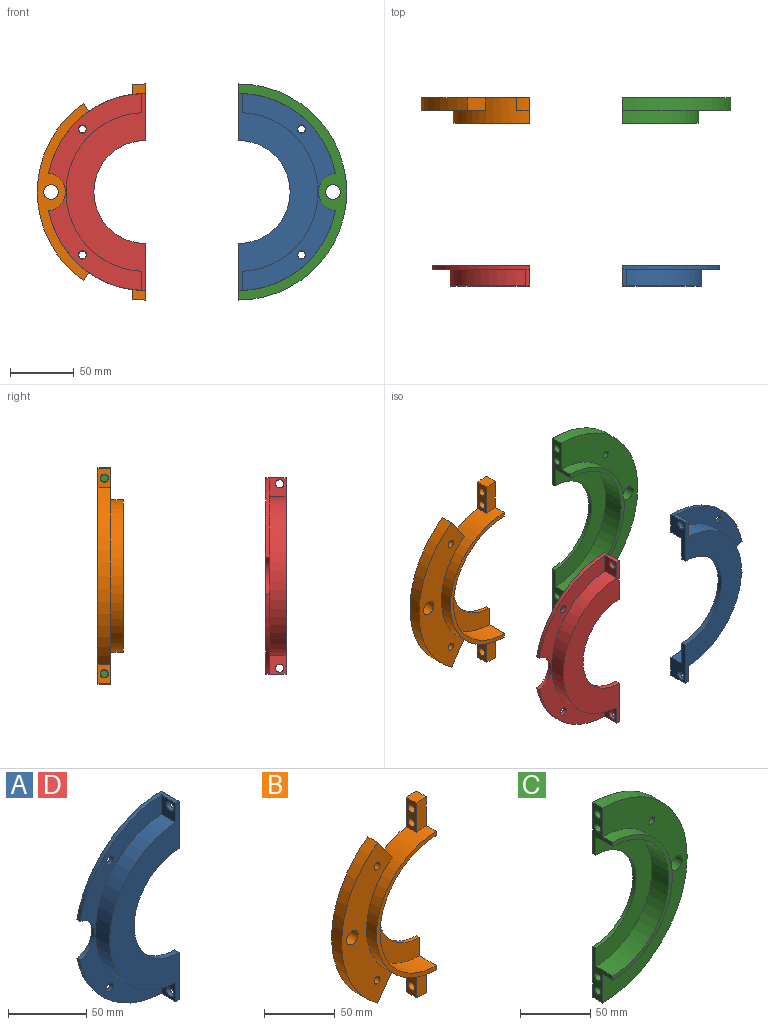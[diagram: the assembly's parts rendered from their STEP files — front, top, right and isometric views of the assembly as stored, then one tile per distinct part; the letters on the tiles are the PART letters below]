
ASSEMBLY  parts=4 mates=7
PART A: 22 faces, bbox 76.1x16x155 mm
  f0: plane 3x0.06mm, normal (0,-1,0), area 0mm2, adj f5,f19
  f1: plane 154.88x73.06mm, normal (0,-1,0), area 2813.3mm2, adj f3,f4,f5,f13,f14,f15,f16,f18
  f2: plane 3x0.06mm, normal (0,-1,0), area 0mm2, adj f4,f17
  f3: cylinder r=62.5mm len=124.86mm, axis (0,-1,0), area 2474.5mm2, adj f1,f6,f16,f18
  f4: cylinder r=77.5mm len=76.06mm, axis (0,1,0), area 320.2mm2, adj f1,f2,f8,f11,f13
  f5: cylinder r=77.5mm len=76.06mm, axis (0,1,0), area 320.2mm2, adj f0,f1,f8,f12,f13
  f6: plane 155x62.5mm, normal (0,-1,0), area 3649.4mm2, adj f3,f7,f11,f12,f16,f17,f18,f19
  f7: cylinder r=40.5mm len=81mm, axis (0,1,0), area 508.9mm2, adj f6,f10,f11,f12
  f8: plane 155x76.06mm, normal (0,1,0), area 3337.2mm2, adj f4,f5,f9,f11,f12,f13,f14,f15
  f9: cylinder r=60.25mm len=120.5mm, axis (0,1,0), area 2271.4mm2, adj f8,f10,f11,f12
  f10: plane 120.5x60.25mm, normal (0,1,0), area 3125.6mm2, adj f7,f9,f11,f12
  f11: plane 37x16mm, normal (1,0,0), area 321.8mm2, adj f4,f6,f7,f8,f9,f10,f17,f21
  f12: plane 37x16mm, normal (1,0,0), area 321.8mm2, adj f5,f6,f7,f8,f9,f10,f19,f20
  f13: cylinder r=15mm len=29.79mm, axis (0,-1,0), area 130.7mm2, adj f1,f4,f5,f8
  f14: cylinder r=3.25mm len=6.5mm, axis (0,-1,0), area 61.3mm2, adj f1,f8
  f15: cylinder r=3.25mm len=6.5mm, axis (0,-1,0), area 61.3mm2, adj f1,f8
  f16: plane 15.01x13mm, normal (-1,0,0), area 162mm2, adj f1,f3,f6,f17,f21
  f17: plane 13x3mm, normal (-0.02,0,1), area 39mm2, adj f2,f6,f11,f16
  f18: plane 15.01x13mm, normal (-1,0,0), area 162mm2, adj f1,f3,f6,f19,f20
  f19: plane 13x3mm, normal (-0.02,0,-1), area 39mm2, adj f0,f6,f12,f18
  f20: cylinder r=3.25mm len=6.5mm, axis (1,0,0), area 61.3mm2, adj f12,f18
  f21: cylinder r=3.25mm len=6.5mm, axis (1,0,0), area 61.3mm2, adj f11,f16
PART B: 25 faces, bbox 85x20x170 mm
  f0: cylinder r=85mm len=139.26mm, axis (0,1,0), area 1631.9mm2, adj f2,f4,f18,f19
  f1: cylinder r=85mm len=10mm, axis (0,1,0), area 100.2mm2, adj f3,f4,f6,f17
  f2: plane 139.26x50.59mm, normal (0,-1,0), area 3319.3mm2, adj f0,f9,f10,f11,f13,f18,f19
  f3: plane 25.84x10mm, normal (0,-1,0), area 250.8mm2, adj f1,f6,f13,f17
  f4: plane 170x85mm, normal (0,1,0), area 6899.3mm2, adj f0,f1,f5,f6,f7,f8,f9,f10
  f5: plane 44.5x20mm, normal (1,0,0), area 301.6mm2, adj f4,f7,f8,f12,f13,f14,f15,f16
  f6: plane 44.5x20mm, normal (1,0,0), area 301.6mm2, adj f1,f3,f4,f7,f13,f14,f15,f16
  f7: cylinder r=40.5mm len=81mm, axis (0,1,0), area 381.7mm2, adj f4,f5,f6,f16
  f8: cylinder r=85mm len=10mm, axis (0,1,0), area 100.2mm2, adj f4,f5,f12,f20
  f9: cylinder r=3mm len=10mm, axis (0,1,0), area 188.5mm2, adj f2,f4
  f10: cylinder r=5.75mm len=11.5mm, axis (0,1,0), area 361.3mm2, adj f2,f4
  f11: cylinder r=3mm len=10mm, axis (0,1,0), area 188.5mm2, adj f2,f4
  f12: plane 25.84x10mm, normal (0,-1,0), area 250.8mm2, adj f5,f8,f13,f20
  f13: cylinder r=60mm len=120mm, axis (0,1,0), area 2417.1mm2, adj f2,f3,f4,f5,f6,f12,f14,f17
  f14: plane 120x60mm, normal (0,-1,0), area 640.5mm2, adj f5,f6,f13,f15
  f15: cylinder r=56.5mm len=113mm, axis (0,-1,0), area 3017.5mm2, adj f5,f6,f14,f16
  f16: plane 113x56.5mm, normal (0,-1,0), area 2437.9mm2, adj f5,f6,f7,f15
  f17: plane 25.25x10mm, normal (-1,0,0), area 186.1mm2, adj f1,f3,f4,f13,f23,f24
  f18: plane 20.48x14.34mm, normal (0.82,0,-0.57), area 250mm2, adj f0,f2,f4,f13
  f19: plane 20.48x14.34mm, normal (0.82,0,0.57), area 250mm2, adj f0,f2,f4,f13
  f20: plane 25.25x10mm, normal (-1,0,0), area 186.1mm2, adj f4,f8,f12,f13,f21,f22
  f21: cylinder r=3.25mm len=10mm, axis (1,0,0), area 204.2mm2, adj f5,f20
  f22: cylinder r=3.25mm len=10mm, axis (1,0,0), area 204.2mm2, adj f5,f20
  f23: cylinder r=3.25mm len=10mm, axis (1,0,0), area 204.2mm2, adj f6,f17
  f24: cylinder r=3.25mm len=10mm, axis (1,0,0), area 204.2mm2, adj f6,f17
PART C: 21 faces, bbox 85x20x170 mm
  f0: plane 44.5x20mm, normal (-1,0,0), area 311.5mm2, adj f1,f2,f7,f8,f9,f10,f11,f12
  f1: cylinder r=40.5mm len=81mm, axis (0,1,0), area 381.7mm2, adj f0,f3,f8,f12
  f2: cylinder r=85mm len=170mm, axis (0,1,0), area 2670.4mm2, adj f0,f3,f7,f8
  f3: plane 44.5x20mm, normal (-1,0,0), area 311.5mm2, adj f1,f2,f7,f8,f9,f10,f11,f12
  f4: cylinder r=5.75mm len=11.5mm, axis (0,1,0), area 361.3mm2, adj f7,f8
  f5: cylinder r=3mm len=10mm, axis (0,1,0), area 188.5mm2, adj f7,f8
  f6: cylinder r=3mm len=10mm, axis (0,1,0), area 188.5mm2, adj f7,f8
  f7: plane 170x85mm, normal (0,-1,0), area 5533.7mm2, adj f0,f2,f3,f4,f5,f6,f9
  f8: plane 170x85mm, normal (0,1,0), area 8612.1mm2, adj f0,f1,f2,f3,f4,f5,f6
  f9: cylinder r=60mm len=120mm, axis (0,1,0), area 1885mm2, adj f0,f3,f7,f10
  f10: plane 120x60mm, normal (0,-1,0), area 640.5mm2, adj f0,f3,f9,f11
  f11: cylinder r=56.5mm len=113mm, axis (0,-1,0), area 3017.5mm2, adj f0,f3,f10,f12
  f12: plane 113x56.5mm, normal (0,-1,0), area 2437.9mm2, adj f0,f1,f3,f11
  f13: cylinder r=3mm len=20mm, axis (-1,0,0), area 377mm2, adj f3,f14
  f14: plane 6x6mm, normal (-1,0,0), area 28.3mm2, adj f13
  f15: cylinder r=3mm len=20mm, axis (-1,0,0), area 377mm2, adj f3,f16
  f16: plane 6x6mm, normal (-1,0,0), area 28.3mm2, adj f15
  f17: cylinder r=3mm len=20mm, axis (-1,0,0), area 377mm2, adj f0,f18
  f18: plane 6x6mm, normal (-1,0,0), area 28.3mm2, adj f17
  f19: cylinder r=3mm len=20mm, axis (-1,0,0), area 377mm2, adj f0,f20
  f20: plane 6x6mm, normal (-1,0,0), area 28.3mm2, adj f19
PART D: same geometry as A
PLACE A rot(axis=(0,1,0),180deg) t=(165.07,-127.15,37.54)mm
PLACE B t=(91.67,4.83,37.54)mm fixed
PLACE C t=(165.07,4.83,37.54)mm
PLACE D t=(91.67,-127.15,37.54)mm
MATE slider A.f20 <-> D.f21  axis (-1,0,0) through (165.07,-138.15,110.04)mm
MATE cylindrical B.f21 <-> C.f15  axis (1,0,0) through (91.67,-0.17,114.54)mm
MATE slider A.f21 <-> D.f20  axis (-1,0,0) through (165.07,-138.15,-34.96)mm
MATE slider C.f19 <-> B.f24  axis (-1,0,0) through (165.07,-0.17,-39.46)mm
MATE slider C.f15 <-> B.f21  axis (-1,0,0) through (165.07,-0.17,114.54)mm
MATE slider B.f7 <-> D.f9  axis (0,-1,0) through (91.67,1.83,37.54)mm
MATE slider A.f9 <-> C.f1  axis (0,1,0) through (165.07,-127.15,37.54)mm
